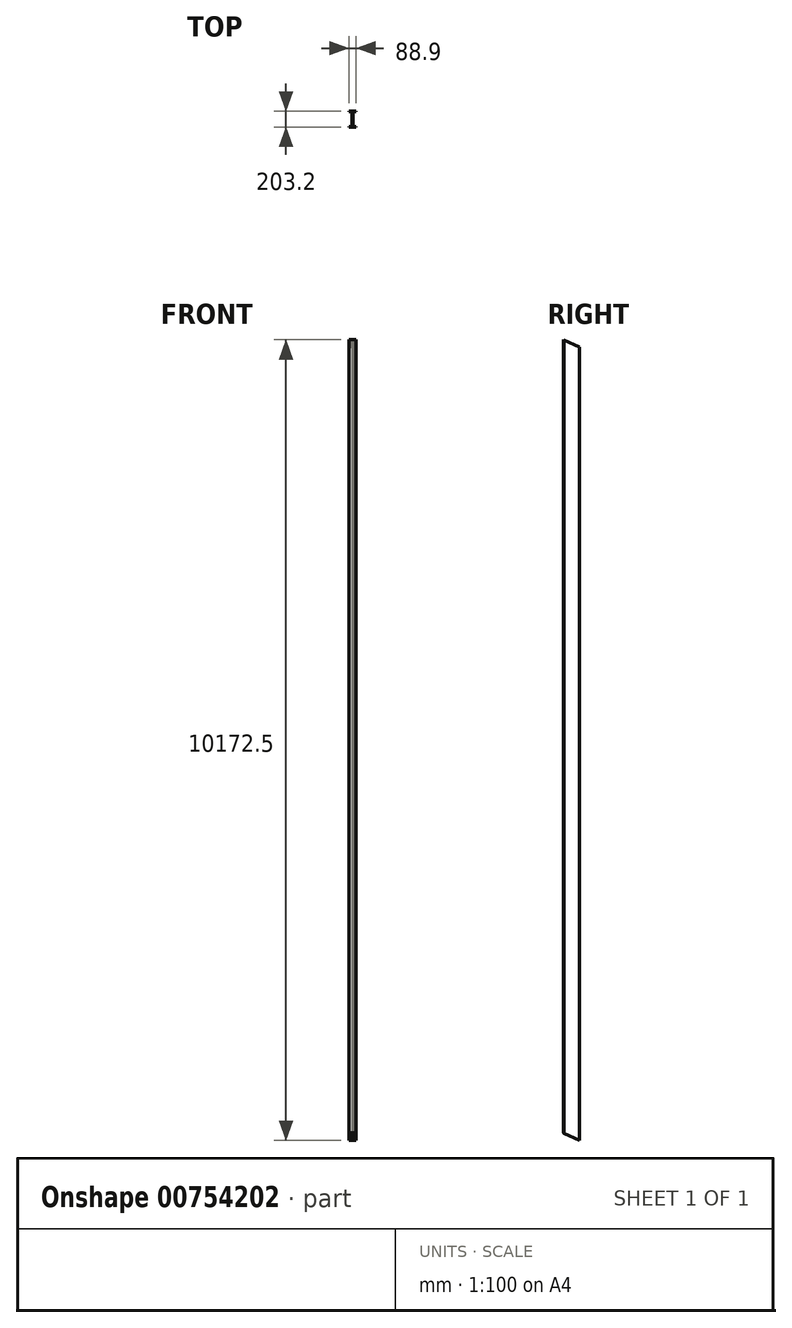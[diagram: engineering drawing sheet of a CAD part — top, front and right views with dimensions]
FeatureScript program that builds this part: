
annotation { "Feature Type Name" : "Feature", "Feature Type Description" : "" }
export const myFeature = defineFeature(function(context is Context, id is Id, definition is map)
    precondition{}
    {
        {
            var Q0;
            Q0=qCreatedBy(makeId("Top.planeOp"),FACE);
            var sketch = newSketch(context, id + "F0", { "sketchPlane" : qUnion([Q0])});
            skLineSegment(sketch, "E0.bottom", {"start": v(44.45, 101.6) * mm, "end": v(-44.45, 101.6) * mm});
            skLineSegment(sketch, "E0.top", {"start": v(44.45, -101.6) * mm, "end": v(-44.45, -101.6) * mm});
            skLineSegment(sketch, "E0.left", {"start": v(44.45, 101.6) * mm, "end": v(44.45, -101.6) * mm});
            skLineSegment(sketch, "E0.right", {"start": v(-44.45, 101.6) * mm, "end": v(-44.45, -101.6) * mm});
            skPoint(sketch, "E0.middle", {"position": v(0, 0) * mm});
            skSolve(sketch);
        }
        {
            var Q0;
            Q0=makeQuery(id+"F0.imprint","IMPRINT",FACE,{"disambiguationData":[TD([[makeQuery(id+"F0.imprint","IMPRINT",EDGE,{"derivedFrom":sQuery(id+"F0.wireOp",EDGE,"E0.bottom")}),1.0]])]});
            extrude(context, id + "F1", {"entities" : qUnion([Q0]), "depth" : 10668 * mm, "offsetDistance" : 25.4 * mm});
        }
        {
            var Q0;
            Q0=qCreatedBy(makeId("Top.planeOp"),FACE);
            var sketch = newSketch(context, id + "F2", { "sketchPlane" : qUnion([Q0])});
            skLineSegment(sketch, "E1.0.0", {"start": v(44.45, -101.6) * mm, "end": v(-44.45, -101.6) * mm, "construction": true});
            skLineSegment(sketch, "E1.0.1", {"start": v(-44.45, -101.6) * mm, "end": v(-44.45, 101.6) * mm, "construction": true});
            skLineSegment(sketch, "E1.0.2", {"start": v(-44.45, 101.6) * mm, "end": v(44.45, 101.6) * mm, "construction": true});
            skLineSegment(sketch, "E1.0.3", {"start": v(44.45, 101.6) * mm, "end": v(44.45, -101.6) * mm, "construction": true});
            skLineSegment(sketch, "E2.bottom", {"start": v(-44.45, -96.52) * mm, "end": v(-4.76, -96.52) * mm});
            skLineSegment(sketch, "E2.top", {"start": v(-44.45, 96.52) * mm, "end": v(-4.76, 96.52) * mm});
            skLineSegment(sketch, "E2.left", {"start": v(-44.45, -96.52) * mm, "end": v(-44.45, 96.52) * mm});
            skLineSegment(sketch, "E2.right", {"start": v(-4.76, -96.52) * mm, "end": v(-4.76, 96.52) * mm});
            skLineSegment(sketch, "E3.bottom", {"start": v(44.45, -96.52) * mm, "end": v(4.76, -96.52) * mm});
            skLineSegment(sketch, "E3.top", {"start": v(44.45, 96.52) * mm, "end": v(4.76, 96.52) * mm});
            skLineSegment(sketch, "E3.left", {"start": v(44.45, -96.52) * mm, "end": v(44.45, 96.52) * mm});
            skLineSegment(sketch, "E3.right", {"start": v(4.76, -96.52) * mm, "end": v(4.76, 96.52) * mm});
            skSolve(sketch);
        }
        {
            var Q0;
            Q0=makeQuery(id+"F2.imprint","IMPRINT",FACE,{"disambiguationData":[TD([[makeQuery(id+"F2.imprint","IMPRINT",EDGE,{"derivedFrom":sQuery(id+"F2.wireOp",EDGE,"E2.bottom")}),1.0]])]});
            var Q1;
            Q1=makeQuery(id+"F2.imprint","IMPRINT",FACE,{"disambiguationData":[TD([[makeQuery(id+"F2.imprint","IMPRINT",EDGE,{"derivedFrom":sQuery(id+"F2.wireOp",EDGE,"E3.bottom")}),-1.0]])]});
            extrude(context, id + "F3", {"entities" : qUnion([Q0, Q1]), "operationType" : NewBodyOperationType.REMOVE, "endBound" : BoundingType.THROUGH_ALL, "depth" : 25.4 * mm, "offsetDistance" : 25.4 * mm});
        }
        {
            var Q0;
            Q0=qCreatedBy(makeId("Right.planeOp"),FACE);
            var sketch = newSketch(context, id + "F4", { "sketchPlane" : qUnion([Q0])});
            skLineSegment(sketch, "E4.0", {"start": v(-96.52, 0) * mm, "end": v(96.52, 0) * mm, "construction": true});
            skLineSegment(sketch, "E5.0.1", {"start": v(101.6, 0) * mm, "end": v(101.6, 10668) * mm});
            skLineSegment(sketch, "E5.0.3", {"start": v(101.6, 10668) * mm, "end": v(101.6, 0) * mm});
            skLineSegment(sketch, "E6.0", {"start": v(-101.6, 10668) * mm, "end": v(-101.6, 0) * mm});
            skLineSegment(sketch, "E7", {"start": v(-101.6, 94.18) * mm, "end": v(4526.27, -2050.72) * mm});
            skLineSegment(sketch, "E8", {"start": v(-101.6, 94.18) * mm, "end": v(-101.6, 0) * mm});
            skLineSegment(sketch, "E9", {"start": v(-101.6, 0) * mm, "end": v(101.6, 0) * mm});
            skLineSegment(sketch, "E10", {"start": v(4526.27, -2050.72) * mm, "end": v(8371.38, 6245.53) * mm});
            skLineSegment(sketch, "E11", {"start": v(8371.38, 6245.53) * mm, "end": v(-101.6, 10172.55) * mm});
            skLineSegment(sketch, "E12", {"start": v(-101.6, 10172.55) * mm, "end": v(-101.6, 0) * mm});
            skSolve(sketch);
        }
        {
            var Q0;
            {var subQ3=sQuery(id+"F4.wireOp",EDGE,"E11");var subQ5=sQuery(id+"F4.wireOp",EDGE,"E12");var subQ7=makeQuery(id+"F4.imprint","INTERSECT",VERTEX,{"derivedFrom":[subQ3,subQ5]});Q0=makeQuery(id+"F4.imprint","IMPRINT",FACE,{"disambiguationData":[TD([[makeQuery(id+"F4.imprint","IMPRINT",EDGE,{"disambiguationData":[TD([[subQ7,1.0]])],"derivedFrom":subQ3}),1.0]])]});}
            extrude(context, id + "F5", {"entities" : qUnion([Q0]), "operationType" : NewBodyOperationType.INTERSECT, "endBound" : BoundingType.SYMMETRIC, "depth" : 127 * mm, "offsetDistance" : 25.4 * mm});
        }
    });
